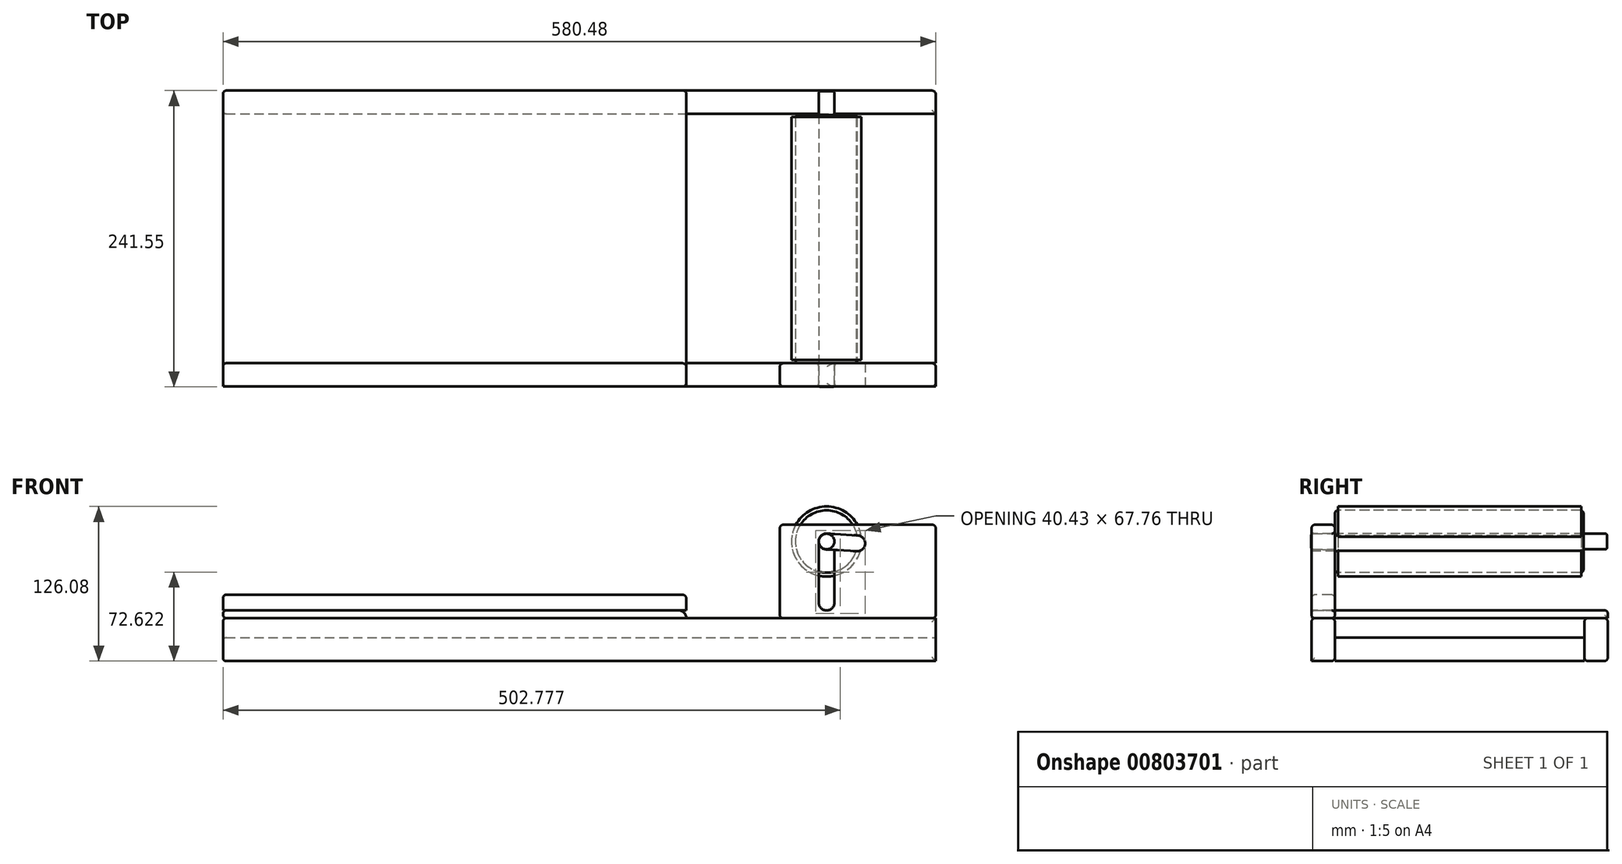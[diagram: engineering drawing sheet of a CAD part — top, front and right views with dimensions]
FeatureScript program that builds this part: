
annotation { "Feature Type Name" : "Feature", "Feature Type Description" : "" }
export const myFeature = defineFeature(function(context is Context, id is Id, definition is map)
    precondition{}
    {
        {
            var Q0;
            Q0=qCreatedBy(makeId("Top.planeOp"),FACE);
            var sketch = newSketch(context, id + "F0", { "sketchPlane" : qUnion([Q0])});
            skLineSegment(sketch, "E0.bottom", {"start": v(-381, 101.6) * mm, "end": v(381, 101.6) * mm});
            skLineSegment(sketch, "E0.top", {"start": v(-381, -101.6) * mm, "end": v(381, -101.6) * mm});
            skLineSegment(sketch, "E0.left", {"start": v(-381, 101.6) * mm, "end": v(-381, -101.6) * mm});
            skLineSegment(sketch, "E0.right", {"start": v(381, 101.6) * mm, "end": v(381, -101.6) * mm});
            skSolve(sketch);
        }
        {
            var Q0;
            Q0 = qSketchRegion(id + "F0", true);
            extrude(context, id + "F1", {"entities" : qUnion([Q0]), "depth" : 19.05 * mm, "offsetDistance" : 25.4 * mm});
        }
        {
            var Q0;
            Q0=makeQuery(id+"F1.opExtrude","CAP_FACE",FACE,{"disambiguationData":[OSD([sQuery(id+"F0.wireOp",EDGE,"E0.bottom"),sQuery(id+"F0.wireOp",EDGE,"E0.top"),sQuery(id+"F0.wireOp",EDGE,"E0.left"),sQuery(id+"F0.wireOp",EDGE,"E0.right")])],"isStart":true});
            var sketch = newSketch(context, id + "F2", { "sketchPlane" : qUnion([Q0])});
            skLineSegment(sketch, "E1", {"start": v(-381, 101.6) * mm, "end": v(-381, 120.65) * mm});
            skLineSegment(sketch, "E2", {"start": v(-381, 120.65) * mm, "end": v(381, 120.65) * mm});
            skLineSegment(sketch, "E3", {"start": v(381, 120.65) * mm, "end": v(381, 101.6) * mm});
            skLineSegment(sketch, "E4", {"start": v(381, 101.6) * mm, "end": v(-381, 101.6) * mm});
            skSolve(sketch);
        }
        {
            var Q0;
            Q0 = qSketchRegion(id + "F2", true);
            extrude(context, id + "F3", {"entities" : qUnion([Q0]), "oppositeDirection" : true, "depth" : 35.05 * mm, "offsetDistance" : 25.4 * mm});
        }
        {
            var Q0;
            Q0=makeQuery(id+"F3.opExtrude","CAP_FACE",FACE,{"disambiguationData":[OSD([sQuery(id+"F2.wireOp",EDGE,"E1"),sQuery(id+"F2.wireOp",EDGE,"E2"),sQuery(id+"F2.wireOp",EDGE,"E3"),sQuery(id+"F2.wireOp",EDGE,"E4")])],"isStart":false});
            var sketch = newSketch(context, id + "F4", { "sketchPlane" : qUnion([Q0])});
            skLineSegment(sketch, "E5", {"start": v(381, -101.6) * mm, "end": v(254, -101.6) * mm});
            skLineSegment(sketch, "E6", {"start": v(254, -101.6) * mm, "end": v(254, -120.65) * mm});
            skLineSegment(sketch, "E7", {"start": v(254, -120.65) * mm, "end": v(381, -120.65) * mm});
            skLineSegment(sketch, "E8", {"start": v(381, -120.65) * mm, "end": v(381, -101.6) * mm});
            skSolve(sketch);
        }
        {
            var Q0;
            Q0 = qSketchRegion(id + "F4", true);
            extrude(context, id + "F5", {"entities" : qUnion([Q0]), "depth" : 76.2 * mm, "offsetDistance" : 25.4 * mm});
        }
        {
            var Q0;
            Q0=makeQuery(id+"F3.boolean.opBoolean","MERGE",FACE,{"derivedFrom":[makeQuery(id+"F1.opExtrude","CAP_FACE",FACE,{"disambiguationData":[OSD([sQuery(id+"F0.wireOp",EDGE,"E0.bottom"),sQuery(id+"F0.wireOp",EDGE,"E0.top"),sQuery(id+"F0.wireOp",EDGE,"E0.left"),sQuery(id+"F0.wireOp",EDGE,"E0.right")])],"isStart":true}),makeQuery(id+"F3.opExtrude","CAP_FACE",FACE,{"disambiguationData":[OSD([sQuery(id+"F2.wireOp",EDGE,"E1"),sQuery(id+"F2.wireOp",EDGE,"E2"),sQuery(id+"F2.wireOp",EDGE,"E3"),sQuery(id+"F2.wireOp",EDGE,"E4")])],"isStart":true})]});
            var sketch = newSketch(context, id + "F6", { "sketchPlane" : qUnion([Q0])});
            skLineSegment(sketch, "E9", {"start": v(381, -101.6) * mm, "end": v(254, -101.6) * mm});
            skLineSegment(sketch, "E10", {"start": v(254, -101.6) * mm, "end": v(254, -120.65) * mm});
            skLineSegment(sketch, "E11", {"start": v(254, -120.65) * mm, "end": v(381, -120.65) * mm});
            skLineSegment(sketch, "E12", {"start": v(381, -120.65) * mm, "end": v(381, -101.6) * mm});
            skSolve(sketch);
        }
        {
            var Q0;
            Q0 = qSketchRegion(id + "F6", true);
            extrude(context, id + "F7", {"entities" : qUnion([Q0]), "oppositeDirection" : true, "depth" : 111.25 * mm, "offsetDistance" : 25.4 * mm});
        }
        {
            var Q0;
            Q0=makeQuery(id+"F3.boolean.opBoolean","MERGE",FACE,{"derivedFrom":[makeQuery(id+"F1.opExtrude","CAP_FACE",FACE,{"disambiguationData":[OSD([sQuery(id+"F0.wireOp",EDGE,"E0.bottom"),sQuery(id+"F0.wireOp",EDGE,"E0.top"),sQuery(id+"F0.wireOp",EDGE,"E0.left"),sQuery(id+"F0.wireOp",EDGE,"E0.right")])],"isStart":true}),makeQuery(id+"F3.opExtrude","CAP_FACE",FACE,{"disambiguationData":[OSD([sQuery(id+"F2.wireOp",EDGE,"E1"),sQuery(id+"F2.wireOp",EDGE,"E2"),sQuery(id+"F2.wireOp",EDGE,"E3"),sQuery(id+"F2.wireOp",EDGE,"E4")])],"isStart":true})]});
            var sketch = newSketch(context, id + "F8", { "sketchPlane" : qUnion([Q0])});
            skLineSegment(sketch, "E13", {"start": v(-381, -101.6) * mm, "end": v(-381, -120.65) * mm});
            skLineSegment(sketch, "E14", {"start": v(-381, -120.65) * mm, "end": v(381, -120.65) * mm});
            skLineSegment(sketch, "E15", {"start": v(381, -120.65) * mm, "end": v(381, -101.6) * mm});
            skLineSegment(sketch, "E16", {"start": v(381, -101.6) * mm, "end": v(-381, -101.6) * mm});
            skSolve(sketch);
        }
        {
            var Q0;
            Q0 = qSketchRegion(id + "F8", true);
            extrude(context, id + "F9", {"entities" : qUnion([Q0]), "oppositeDirection" : true, "depth" : 35.05 * mm, "offsetDistance" : 25.4 * mm});
        }
        {
            var Q0;
            Q0=makeQuery(id+"F9.opExtrude","CAP_FACE",FACE,{"disambiguationData":[OSD([sQuery(id+"F8.wireOp",EDGE,"E13"),sQuery(id+"F8.wireOp",EDGE,"E14"),sQuery(id+"F8.wireOp",EDGE,"E15"),sQuery(id+"F8.wireOp",EDGE,"E16")])],"isStart":false});
            var sketch = newSketch(context, id + "F10", { "sketchPlane" : qUnion([Q0])});
            skLineSegment(sketch, "E17", {"start": v(-381, 120.65) * mm, "end": v(-381, -120.65) * mm});
            skLineSegment(sketch, "E18", {"start": v(-381, -120.65) * mm, "end": v(177.8, -120.65) * mm});
            skLineSegment(sketch, "E19", {"start": v(177.8, -120.65) * mm, "end": v(177.8, 120.65) * mm});
            skLineSegment(sketch, "E20", {"start": v(177.8, 120.65) * mm, "end": v(-381, 120.65) * mm});
            skSolve(sketch);
        }
        {
            var Q0;
            Q0 = qSketchRegion(id + "F10", true);
            extrude(context, id + "F11", {"entities" : qUnion([Q0]), "depth" : 6.35 * mm, "offsetDistance" : 25.4 * mm});
        }
        {
            var Q0;
            Q0=makeQuery(id+"F11.opExtrude","CAP_FACE",FACE,{"disambiguationData":[OSD([sQuery(id+"F10.wireOp",EDGE,"E17"),sQuery(id+"F10.wireOp",EDGE,"E18"),sQuery(id+"F10.wireOp",EDGE,"E19"),sQuery(id+"F10.wireOp",EDGE,"E20")])],"isStart":false});
            var sketch = newSketch(context, id + "F12", { "sketchPlane" : qUnion([Q0])});
            skLineSegment(sketch, "E21", {"start": v(-381, -120.65) * mm, "end": v(-381, -101.6) * mm});
            skLineSegment(sketch, "E22", {"start": v(-381, -101.6) * mm, "end": v(177.8, -101.6) * mm});
            skLineSegment(sketch, "E23", {"start": v(177.8, -101.6) * mm, "end": v(177.8, -120.65) * mm});
            skLineSegment(sketch, "E24", {"start": v(177.8, -120.65) * mm, "end": v(-381, -120.65) * mm});
            skSolve(sketch);
        }
        {
            var Q0;
            Q0 = qSketchRegion(id + "F12", true);
            extrude(context, id + "F13", {"entities" : qUnion([Q0]), "depth" : 12.7 * mm, "offsetDistance" : 25.4 * mm});
        }
        {
            var Q0;
            Q0=makeQuery(id+"F11.opExtrude","CAP_EDGE",EDGE,{"disambiguationData":[OSD([sQuery(id+"F10.wireOp",EDGE,"E19")])],"isStart":false});
            fillet(context, id + "F14", {"entities" : qUnion([Q0]), "radius" : 6.35 * mm, "tangentPropagation" : true, "allowEdgeOverflow" : false});
        }
        {
            var Q0;
            Q0=makeQuery(id+"F5.opExtrude","CAP_EDGE",EDGE,{"disambiguationData":[OSD([sQuery(id+"F4.wireOp",EDGE,"E7")])],"isStart":false});
            var Q1;
            Q1=makeQuery(id+"F5.opExtrude","SWEPT_EDGE",EDGE,{"disambiguationData":[OSD([sQuery(id+"F2.wireOp",EDGE,"E2"),sQuery(id+"F4.wireOp",EDGE,"E6"),sQuery(id+"F4.wireOp",EDGE,"E7")])]});
            var Q2;
            Q2=makeQuery(id+"F5.opExtrude","SWEPT_EDGE",EDGE,{"disambiguationData":[OSD([sQuery(id+"F4.wireOp",EDGE,"E7"),sQuery(id+"F4.wireOp",EDGE,"E8")])]});
            var Q3;
            Q3=makeQuery(id+"F7.opExtrude","SWEPT_EDGE",EDGE,{"disambiguationData":[OSD([sQuery(id+"F0.wireOp",EDGE,"E0.right"),sQuery(id+"F2.wireOp",EDGE,"E3"),sQuery(id+"F6.wireOp",EDGE,"E9"),sQuery(id+"F6.wireOp",EDGE,"E12")])]});
            var Q4;
            Q4=makeQuery(id+"F7.opExtrude","CAP_EDGE",EDGE,{"disambiguationData":[OSD([sQuery(id+"F6.wireOp",EDGE,"E9")])],"isStart":false});
            var Q5;
            Q5=makeQuery(id+"F7.opExtrude","SWEPT_EDGE",EDGE,{"disambiguationData":[OSD([sQuery(id+"F0.wireOp",EDGE,"E0.bottom"),sQuery(id+"F6.wireOp",EDGE,"E9"),sQuery(id+"F6.wireOp",EDGE,"E10")])]});
            var Q6;
            Q6=makeQuery(id+"F5.opExtrude","SWEPT_EDGE",EDGE,{"disambiguationData":[OSD([sQuery(id+"F2.wireOp",EDGE,"E4"),sQuery(id+"F4.wireOp",EDGE,"E5"),sQuery(id+"F4.wireOp",EDGE,"E6")])]});
            var Q7;
            Q7=makeQuery(id+"F5.opExtrude","SWEPT_EDGE",EDGE,{"disambiguationData":[OSD([sQuery(id+"F4.wireOp",EDGE,"E5"),sQuery(id+"F4.wireOp",EDGE,"E8")])]});
            var Q8;
            Q8=makeQuery(id+"F5.opExtrude","CAP_EDGE",EDGE,{"disambiguationData":[OSD([sQuery(id+"F4.wireOp",EDGE,"E5")])],"isStart":false});
            var Q9;
            Q9=makeQuery(id+"F7.opExtrude","CAP_EDGE",EDGE,{"disambiguationData":[OSD([sQuery(id+"F6.wireOp",EDGE,"E11")])],"isStart":false});
            var Q10;
            Q10=makeQuery(id+"F7.opExtrude","SWEPT_EDGE",EDGE,{"disambiguationData":[OSD([sQuery(id+"F6.wireOp",EDGE,"E10"),sQuery(id+"F6.wireOp",EDGE,"E11")])]});
            var Q11;
            Q11=makeQuery(id+"F7.opExtrude","SWEPT_EDGE",EDGE,{"disambiguationData":[OSD([sQuery(id+"F6.wireOp",EDGE,"E11"),sQuery(id+"F6.wireOp",EDGE,"E12")])]});
            var Q12;
            Q12=makeQuery(id+"F7.opExtrude","CAP_EDGE",EDGE,{"disambiguationData":[OSD([sQuery(id+"F6.wireOp",EDGE,"E10")])],"isStart":false});
            var Q13;
            Q13=makeQuery(id+"F7.opExtrude","CAP_EDGE",EDGE,{"disambiguationData":[OSD([sQuery(id+"F6.wireOp",EDGE,"E12")])],"isStart":false});
            var Q14;
            Q14=makeQuery(id+"F5.opExtrude","CAP_EDGE",EDGE,{"disambiguationData":[OSD([sQuery(id+"F4.wireOp",EDGE,"E6")])],"isStart":false});
            var Q15;
            Q15=makeQuery(id+"F5.opExtrude","CAP_EDGE",EDGE,{"disambiguationData":[OSD([sQuery(id+"F4.wireOp",EDGE,"E8")])],"isStart":false});
            var Q16;
            Q16=makeQuery(id+"F9.opExtrude","CAP_EDGE",EDGE,{"disambiguationData":[OSD([sQuery(id+"F8.wireOp",EDGE,"E14")])],"isStart":true});
            var Q17;
            Q17=makeQuery(id+"F9.opExtrude","SWEPT_EDGE",EDGE,{"disambiguationData":[OSD([sQuery(id+"F8.wireOp",EDGE,"E14"),sQuery(id+"F8.wireOp",EDGE,"E15")])]});
            var Q18;
            Q18=makeQuery(id+"F3.opExtrude","SWEPT_FACE",FACE,{"disambiguationData":[OSD([sQuery(id+"F2.wireOp",EDGE,"E4")])]});
            var Q19;
            Q19=makeQuery(id+"F3.opExtrude","CAP_EDGE",EDGE,{"disambiguationData":[OSD([sQuery(id+"F2.wireOp",EDGE,"E2")])],"isStart":false});
            var Q20;
            Q20=makeQuery(id+"F9.opExtrude","CAP_EDGE",EDGE,{"disambiguationData":[OSD([sQuery(id+"F8.wireOp",EDGE,"E14")])],"isStart":false});
            var Q21;
            Q21=makeQuery(id+"F9.opExtrude","CAP_EDGE",EDGE,{"disambiguationData":[OSD([sQuery(id+"F8.wireOp",EDGE,"E16")])],"isStart":false});
            var Q22;
            Q22=makeQuery(id+"F13.opExtrude","CAP_EDGE",EDGE,{"disambiguationData":[OSD([sQuery(id+"F12.wireOp",EDGE,"E23")])],"isStart":false});
            var Q23;
            Q23=makeQuery(id+"F13.opExtrude","CAP_EDGE",EDGE,{"disambiguationData":[OSD([sQuery(id+"F12.wireOp",EDGE,"E24")])],"isStart":false});
            var Q24;
            Q24=makeQuery(id+"F13.opExtrude","SWEPT_EDGE",EDGE,{"disambiguationData":[OSD([sQuery(id+"F12.wireOp",EDGE,"E23"),sQuery(id+"F12.wireOp",EDGE,"E24")])]});
            var Q25;
            Q25=makeQuery(id+"F13.opExtrude","SWEPT_EDGE",EDGE,{"disambiguationData":[OSD([sQuery(id+"F10.wireOp",EDGE,"E19"),sQuery(id+"F12.wireOp",EDGE,"E22"),sQuery(id+"F12.wireOp",EDGE,"E23")])]});
            var Q26;
            Q26=makeQuery(id+"F11.opExtrude","CAP_EDGE",EDGE,{"disambiguationData":[OSD([sQuery(id+"F10.wireOp",EDGE,"E17")])],"isStart":false});
            var Q27;
            Q27=makeQuery(id+"F9.opExtrude","SWEPT_EDGE",EDGE,{"disambiguationData":[OSD([sQuery(id+"F0.wireOp",EDGE,"E0.left"),sQuery(id+"F2.wireOp",EDGE,"E1"),sQuery(id+"F8.wireOp",EDGE,"E13"),sQuery(id+"F8.wireOp",EDGE,"E16")])]});
            var Q28;
            Q28=makeQuery(id+"F9.opExtrude","SWEPT_EDGE",EDGE,{"disambiguationData":[OSD([sQuery(id+"F8.wireOp",EDGE,"E13"),sQuery(id+"F8.wireOp",EDGE,"E14")])]});
            var Q29;
            Q29=makeQuery(id+"F9.opExtrude","CAP_FACE",FACE,{"disambiguationData":[OSD([sQuery(id+"F8.wireOp",EDGE,"E13"),sQuery(id+"F8.wireOp",EDGE,"E14"),sQuery(id+"F8.wireOp",EDGE,"E15"),sQuery(id+"F8.wireOp",EDGE,"E16")])],"isStart":true});
            var Q30;
            Q30=makeQuery(id+"F13.opExtrude","CAP_EDGE",EDGE,{"disambiguationData":[OSD([sQuery(id+"F12.wireOp",EDGE,"E22")])],"isStart":false});
            fillet(context, id + "F15", {"entities" : qUnion([Q0, Q1, Q2, Q3, Q4, Q5, Q6, Q7, Q8, Q9, Q10, Q11, Q12, Q13, Q14, Q15, Q16, Q17, Q18, Q19, Q20, Q21, Q22, Q23, Q24, Q25, Q26, Q27, Q28, Q29, Q30]), "radius" : 3.05 * mm, "tangentPropagation" : true, "allowEdgeOverflow" : false});
        }
        {
            var Q0;
            Q0=makeQuery(id+"F5.opExtrude","SWEPT_FACE",FACE,{"disambiguationData":[OSD([sQuery(id+"F4.wireOp",EDGE,"E7")])]});
            var sketch = newSketch(context, id + "F16", { "sketchPlane" : qUnion([Q0])});
            skArc(sketch, "E25", {"start": v(298.58, 97.5) * mm, "mid": v(292.1, 103.98) * mm, "end": v(285.62, 97.5) * mm});
            skArc(sketch, "E26", {"start": v(285.62, 47.76) * mm, "mid": v(292.1, 41.28) * mm, "end": v(298.58, 47.76) * mm});
            skLineSegment(sketch, "E27", {"start": v(285.62, 97.5) * mm, "end": v(285.62, 47.76) * mm});
            skLineSegment(sketch, "E28", {"start": v(298.58, 97.5) * mm, "end": v(298.58, 47.76) * mm});
            skSolve(sketch);
        }
        {
            var Q0;
            Q0 = qSketchRegion(id + "F16", true);
            extrude(context, id + "F17", {"entities" : qUnion([Q0]), "operationType" : NewBodyOperationType.REMOVE, "oppositeDirection" : true, "depth" : 254 * mm, "offsetDistance" : 25.4 * mm});
        }
        {
            var Q0;
            Q0=makeQuery(id+"F5.opExtrude","SWEPT_FACE",FACE,{"disambiguationData":[OSD([sQuery(id+"F4.wireOp",EDGE,"E7")])]});
            var sketch = newSketch(context, id + "F18", { "sketchPlane" : qUnion([Q0])});
            skCircle(sketch, "E29", {"center": v(292.1, 97.5) * mm, "radius": 6.35 * mm});
            skSolve(sketch);
        }
        {
            var Q0;
            Q0 = qSketchRegion(id + "F18", true);
            extrude(context, id + "F19", {"entities" : qUnion([Q0]), "oppositeDirection" : true, "depth" : 241.3 * mm, "offsetDistance" : 25.4 * mm});
        }
        {
            var Q0;
            Q0=makeQuery(id+"F19.opExtrude","CAP_FACE",FACE,{"disambiguationData":[OSD([sQuery(id+"F18.wireOp",EDGE,"E29")])],"isStart":true});
            var Q1;
            Q1=makeQuery(id+"F19.opExtrude","CAP_FACE",FACE,{"disambiguationData":[OSD([sQuery(id+"F18.wireOp",EDGE,"E29")])],"isStart":false});
            fillet(context, id + "F20", {"entities" : qUnion([Q0, Q1]), "radius" : 3.05 * mm, "tangentPropagation" : true, "allowEdgeOverflow" : false});
        }
        {
            var Q0;
            Q0=makeQuery(id+"F5.opExtrude","SWEPT_FACE",FACE,{"disambiguationData":[OSD([sQuery(id+"F4.wireOp",EDGE,"E5")])]});
            var sketch = newSketch(context, id + "F21", { "sketchPlane" : qUnion([Q0])});
            skCircle(sketch, "E30", {"center": v(-292.1, 97.5) * mm, "radius": 25.4 * mm});
            skSolve(sketch);
        }
        {
            var Q0;
            Q0 = qSketchRegion(id + "F21", true);
            extrude(context, id + "F22", {"entities" : qUnion([Q0]), "depth" : 202.44 * mm, "offsetDistance" : 25.4 * mm});
        }
        {
            var Q0;
            Q0=makeQuery(id+"F22.opExtrude","CAP_FACE",FACE,{"disambiguationData":[OSD([sQuery(id+"F21.wireOp",EDGE,"E30")])],"isStart":false});
            fillet(context, id + "F23", {"entities" : qUnion([Q0]), "radius" : 2.54 * mm, "tangentPropagation" : true, "allowEdgeOverflow" : false});
        }
        {
            var Q0;
            Q0=makeQuery(id+"F22.opExtrude","CAP_EDGE",EDGE,{"disambiguationData":[OSD([sQuery(id+"F21.wireOp",EDGE,"E30")])],"isStart":true});
            fillet(context, id + "F24", {"entities" : qUnion([Q0]), "radius" : 2.54 * mm, "tangentPropagation" : true, "allowEdgeOverflow" : false});
        }
        {
            var Q0;
            Q0=makeQuery(id+"F22.opExtrude","CAP_FACE",FACE,{"disambiguationData":[OSD([sQuery(id+"F21.wireOp",EDGE,"E30")])],"isStart":true});
            var sketch = newSketch(context, id + "F25", { "sketchPlane" : qUnion([Q0])});
            skCircle(sketch, "E31", {"center": v(292.1, 97.5) * mm, "radius": 25.4 * mm});
            skCircle(sketch, "E32", {"center": v(292.1, 97.5) * mm, "radius": 28.58 * mm});
            skSolve(sketch);
        }
        {
            var Q0;
            Q0 = qSketchRegion(id + "F25", true);
            extrude(context, id + "F26", {"entities" : qUnion([Q0]), "oppositeDirection" : true, "depth" : 200.66 * mm, "offsetDistance" : 25.4 * mm});
        }
        {
            var Q0;
            Q0=makeQuery(id+"F22.opExtrude","CAP_FACE",FACE,{"disambiguationData":[OSD([sQuery(id+"F21.wireOp",EDGE,"E30")])],"isStart":true});
            var sketch = newSketch(context, id + "F27", { "sketchPlane" : qUnion([Q0])});
            skCircle(sketch, "E33", {"center": v(292.1, 97.5) * mm, "radius": 25.4 * mm});
            skCircle(sketch, "E34", {"center": v(292.1, 97.5) * mm, "radius": 30.03 * mm});
            skSolve(sketch);
        }
        {
            var Q0;
            Q0 = qSketchRegion(id + "F27", true);
            extrude(context, id + "F28", {"entities" : qUnion([Q0]), "operationType" : NewBodyOperationType.REMOVE, "oppositeDirection" : true, "depth" : 2.54 * mm, "offsetDistance" : 25.4 * mm});
        }
        {
            var Q0;
            Q0=makeQuery(id+"F3.opExtrude","SWEPT_FACE",FACE,{"disambiguationData":[OSD([sQuery(id+"F2.wireOp",EDGE,"E2")])]});
            var sketch = newSketch(context, id + "F29", { "sketchPlane" : qUnion([Q0])});
            skLineSegment(sketch, "E35", {"start": v(-402.68, 84.63) * mm, "end": v(-199.48, 84.63) * mm});
            skLineSegment(sketch, "E36", {"start": v(-199.48, 84.63) * mm, "end": v(-199.48, -54.52) * mm});
            skLineSegment(sketch, "E37", {"start": v(-199.48, -54.52) * mm, "end": v(-408.57, -54.52) * mm});
            skLineSegment(sketch, "E38", {"start": v(-408.57, -54.52) * mm, "end": v(-402.68, 84.63) * mm});
            skSolve(sketch);
        }
        {
            var Q0;
            Q0 = qSketchRegion(id + "F29", true);
            extrude(context, id + "F30", {"entities" : qUnion([Q0]), "operationType" : NewBodyOperationType.REMOVE, "oppositeDirection" : true, "depth" : 304.8 * mm, "offsetDistance" : 25.4 * mm});
        }
        {
            var Q0;
            Q0=makeQuery(id+"F30.boolean.opBoolean","INTERSECT",EDGE,{"derivedFrom":[makeQuery(id+"F9.opExtrude","SWEPT_FACE",FACE,{"disambiguationData":[OSD([sQuery(id+"F8.wireOp",EDGE,"E16")])]}),makeQuery(id+"F30.opExtrude","SWEPT_FACE",FACE,{"disambiguationData":[OSD([sQuery(id+"F29.wireOp",EDGE,"E36")])]})]});
            var Q1;
            Q1=makeQuery(id+"F30.boolean.opBoolean","INTERSECT",EDGE,{"derivedFrom":[makeQuery(id+"F1.opExtrude","CAP_FACE",FACE,{"disambiguationData":[OSD([sQuery(id+"F0.wireOp",EDGE,"E0.bottom"),sQuery(id+"F0.wireOp",EDGE,"E0.top"),sQuery(id+"F0.wireOp",EDGE,"E0.left"),sQuery(id+"F0.wireOp",EDGE,"E0.right")])],"isStart":false}),makeQuery(id+"F30.opExtrude","SWEPT_FACE",FACE,{"disambiguationData":[OSD([sQuery(id+"F29.wireOp",EDGE,"E36")])]})]});
            var Q2;
            Q2=makeQuery(id+"F30.boolean.opBoolean","INTERSECT",EDGE,{"derivedFrom":[makeQuery(id+"F3.boolean.opBoolean","MERGE",FACE,{"derivedFrom":[makeQuery(id+"F1.opExtrude","CAP_FACE",FACE,{"disambiguationData":[OSD([sQuery(id+"F0.wireOp",EDGE,"E0.bottom"),sQuery(id+"F0.wireOp",EDGE,"E0.top"),sQuery(id+"F0.wireOp",EDGE,"E0.left"),sQuery(id+"F0.wireOp",EDGE,"E0.right")])],"isStart":true}),makeQuery(id+"F3.opExtrude","CAP_FACE",FACE,{"disambiguationData":[OSD([sQuery(id+"F2.wireOp",EDGE,"E1"),sQuery(id+"F2.wireOp",EDGE,"E2"),sQuery(id+"F2.wireOp",EDGE,"E3"),sQuery(id+"F2.wireOp",EDGE,"E4")])],"isStart":true})]}),makeQuery(id+"F30.opExtrude","SWEPT_FACE",FACE,{"disambiguationData":[OSD([sQuery(id+"F29.wireOp",EDGE,"E36")])]})]});
            var Q3;
            Q3=makeQuery(id+"F30.boolean.opBoolean","INTERSECT",EDGE,{"derivedFrom":[makeQuery(id+"F11.opExtrude","CAP_FACE",FACE,{"disambiguationData":[OSD([sQuery(id+"F10.wireOp",EDGE,"E17"),sQuery(id+"F10.wireOp",EDGE,"E18"),sQuery(id+"F10.wireOp",EDGE,"E19"),sQuery(id+"F10.wireOp",EDGE,"E20")])],"isStart":true}),makeQuery(id+"F30.opExtrude","SWEPT_FACE",FACE,{"disambiguationData":[OSD([sQuery(id+"F29.wireOp",EDGE,"E36")])]})]});
            var Q4;
            Q4=makeQuery(id+"F30.boolean.opBoolean","INTERSECT",EDGE,{"derivedFrom":[makeQuery(id+"F11.opExtrude","CAP_FACE",FACE,{"disambiguationData":[OSD([sQuery(id+"F10.wireOp",EDGE,"E17"),sQuery(id+"F10.wireOp",EDGE,"E18"),sQuery(id+"F10.wireOp",EDGE,"E19"),sQuery(id+"F10.wireOp",EDGE,"E20")])],"isStart":false}),makeQuery(id+"F30.opExtrude","SWEPT_FACE",FACE,{"disambiguationData":[OSD([sQuery(id+"F29.wireOp",EDGE,"E36")])]})]});
            var Q5;
            {var subQ0=sQuery(id+"F29.wireOp",EDGE,"E36");Q5=makeQuery(id+"F30.boolean.opBoolean","COPY",EDGE,{"disambiguationData":[topologyDisambiguationEdgeConnected([makeQuery(id+"F13.opExtrude","SWEPT_FACE",FACE,{"disambiguationData":[OSD([sQuery(id+"F12.wireOp",EDGE,"E24")])]})])],"derivedFrom":makeQuery(id+"F30.opExtrude","CAP_EDGE",EDGE,{"disambiguationData":[OSD([subQ0])],"isStart":true})});}
            var Q6;
            Q6=makeQuery(id+"F30.boolean.opBoolean","INTERSECT",EDGE,{"derivedFrom":[makeQuery(id+"F13.opExtrude","SWEPT_FACE",FACE,{"disambiguationData":[OSD([sQuery(id+"F12.wireOp",EDGE,"E22")])]}),makeQuery(id+"F30.opExtrude","SWEPT_FACE",FACE,{"disambiguationData":[OSD([sQuery(id+"F29.wireOp",EDGE,"E36")])]})]});
            var Q7;
            Q7=makeQuery(id+"F11.opExtrude","CAP_EDGE",EDGE,{"disambiguationData":[OSD([sQuery(id+"F10.wireOp",EDGE,"E20")])],"isStart":false});
            var Q8;
            Q8=makeQuery(id+"F30.boolean.opBoolean","INTERSECT",EDGE,{"derivedFrom":[makeQuery(id+"F11.opExtrude","SWEPT_FACE",FACE,{"disambiguationData":[OSD([sQuery(id+"F10.wireOp",EDGE,"E20")])]}),makeQuery(id+"F30.opExtrude","SWEPT_FACE",FACE,{"disambiguationData":[OSD([sQuery(id+"F29.wireOp",EDGE,"E36")])]})]});
            var Q9;
            {var subQ0=sQuery(id+"F29.wireOp",EDGE,"E36");Q9=makeQuery(id+"F30.boolean.opBoolean","COPY",EDGE,{"disambiguationData":[topologyDisambiguationEdgeConnected([makeQuery(id+"F11.opExtrude","SWEPT_FACE",FACE,{"disambiguationData":[OSD([sQuery(id+"F10.wireOp",EDGE,"E18")])]})])],"derivedFrom":makeQuery(id+"F30.opExtrude","CAP_EDGE",EDGE,{"disambiguationData":[OSD([subQ0])],"isStart":true})});}
            fillet(context, id + "F31", {"entities" : qUnion([Q0, Q1, Q2, Q3, Q4, Q5, Q6, Q7, Q8, Q9]), "radius" : 2.54 * mm, "tangentPropagation" : true, "allowEdgeOverflow" : false});
        }
        {
            var Q0;
            Q0=makeQuery(id+"F7.opExtrude","SWEPT_FACE",FACE,{"disambiguationData":[OSD([sQuery(id+"F6.wireOp",EDGE,"E11")])]});
            var Q1;
            Q1=makeQuery(id+"F7.opExtrude","SWEPT_FACE",FACE,{"disambiguationData":[OSD([sQuery(id+"F6.wireOp",EDGE,"E9")])]});
            var Q2;
            Q2=makeQuery(id+"F5.opExtrude","SWEPT_FACE",FACE,{"disambiguationData":[OSD([sQuery(id+"F4.wireOp",EDGE,"E5")])]});
            var Q3;
            Q3=makeQuery(id+"F5.opExtrude","SWEPT_FACE",FACE,{"disambiguationData":[OSD([sQuery(id+"F4.wireOp",EDGE,"E7")])]});
            fillet(context, id + "F32", {"entities" : qUnion([Q0, Q1, Q2, Q3]), "radius" : 2.54 * mm, "tangentPropagation" : true, "allowEdgeOverflow" : false});
        }
        {
            var Q0;
            Q0=makeQuery(id+"F22.opExtrude","CAP_FACE",FACE,{"disambiguationData":[OSD([sQuery(id+"F21.wireOp",EDGE,"E30")])],"isStart":true});
            var sketch = newSketch(context, id + "F33", { "sketchPlane" : qUnion([Q0])});
            skCircle(sketch, "E39", {"center": v(292.1, 97.5) * mm, "radius": 25.4 * mm});
            skCircle(sketch, "E40", {"center": v(292.1, 97.5) * mm, "radius": 28.58 * mm});
            skSolve(sketch);
        }
        {
            var Q0;
            Q0 = qSketchRegion(id + "F33", true);
            extrude(context, id + "F34", {"entities" : qUnion([Q0]), "oppositeDirection" : true, "depth" : 200.66 * mm, "offsetDistance" : 25.4 * mm});
        }
        {
            var Q0;
            Q0=makeQuery(id+"F34.opExtrude","SWEPT_BODY",BODY,{"disambiguationData":[OSD([sQuery(id+"F33.wireOp",EDGE,"E39"),sQuery(id+"F33.wireOp",EDGE,"E40")])]});
            deleteBodies(context, id + "F35", {"entities" : qUnion([Q0])});
        }
        {
            var Q0;
            Q0=makeQuery(id+"F5.opExtrude","SWEPT_FACE",FACE,{"disambiguationData":[OSD([sQuery(id+"F4.wireOp",EDGE,"E7")])]});
            var sketch = newSketch(context, id + "F36", { "sketchPlane" : qUnion([Q0])});
            skArc(sketch, "E41", {"start": v(292.49, 103.97) * mm, "mid": v(285.63, 97.9) * mm, "end": v(291.71, 91.04) * mm});
            skArc(sketch, "E42", {"start": v(316.66, 89.55) * mm, "mid": v(323.51, 95.62) * mm, "end": v(317.43, 102.48) * mm});
            skLineSegment(sketch, "E43", {"start": v(292.49, 103.97) * mm, "end": v(317.43, 102.48) * mm});
            skLineSegment(sketch, "E44", {"start": v(291.71, 91.04) * mm, "end": v(316.66, 89.55) * mm});
            skSolve(sketch);
        }
        {
            var Q0;
            Q0 = qSketchRegion(id + "F36", true);
            extrude(context, id + "F37", {"entities" : qUnion([Q0]), "operationType" : NewBodyOperationType.REMOVE, "oppositeDirection" : true, "depth" : 254 * mm, "offsetDistance" : 25.4 * mm});
        }
        {
            var Q0;
            Q0=makeQuery(id+"F37.boolean.opBoolean","COPY",EDGE,{"derivedFrom":makeQuery(id+"F37.opExtrude","CAP_EDGE",EDGE,{"disambiguationData":[OSD([sQuery(id+"F36.wireOp",EDGE,"E43")])],"isStart":true})});
            var Q1;
            Q1=makeQuery(id+"F37.boolean.opBoolean","INTERSECT",EDGE,{"derivedFrom":[makeQuery(id+"F7.opExtrude","SWEPT_FACE",FACE,{"disambiguationData":[OSD([sQuery(id+"F6.wireOp",EDGE,"E9")])]}),makeQuery(id+"F37.opExtrude","SWEPT_FACE",FACE,{"disambiguationData":[OSD([sQuery(id+"F36.wireOp",EDGE,"E42")])]})]});
            fillet(context, id + "F38", {"entities" : qUnion([Q0, Q1]), "radius" : 2.54 * mm, "tangentPropagation" : true, "allowEdgeOverflow" : false});
        }
        {
            var Q0;
            Q0=makeQuery(id+"F22.opExtrude","CAP_FACE",FACE,{"disambiguationData":[OSD([sQuery(id+"F21.wireOp",EDGE,"E30")])],"isStart":true});
            var sketch = newSketch(context, id + "F39", { "sketchPlane" : qUnion([Q0])});
            skCircle(sketch, "E45", {"center": v(292.1, 97.5) * mm, "radius": 6.35 * mm});
            skSolve(sketch);
        }
        {
            var Q0;
            Q0 = qSketchRegion(id + "F39", true);
            extrude(context, id + "F40", {"entities" : qUnion([Q0]), "operationType" : NewBodyOperationType.ADD, "depth" : 19.3 * mm, "offsetDistance" : 25.4 * mm});
        }
        {
            var Q0;
            Q0=makeQuery(id+"F40.opExtrude","CAP_FACE",FACE,{"disambiguationData":[OSD([sQuery(id+"F39.wireOp",EDGE,"E45")])],"isStart":false});
            fillet(context, id + "F41", {"entities" : qUnion([Q0]), "radius" : 1.52 * mm, "tangentPropagation" : true, "allowEdgeOverflow" : false});
        }
        {
            var Q0;
            Q0=makeQuery(id+"F22.opExtrude","CAP_FACE",FACE,{"disambiguationData":[OSD([sQuery(id+"F21.wireOp",EDGE,"E30")])],"isStart":false});
            var sketch = newSketch(context, id + "F42", { "sketchPlane" : qUnion([Q0])});
            skCircle(sketch, "E46", {"center": v(-292.1, 97.5) * mm, "radius": 6.35 * mm});
            skSolve(sketch);
        }
        {
            var Q0;
            Q0 = qSketchRegion(id + "F42", true);
            extrude(context, id + "F43", {"entities" : qUnion([Q0]), "operationType" : NewBodyOperationType.ADD, "depth" : 19.3 * mm, "offsetDistance" : 25.4 * mm});
        }
        {
            var Q0;
            Q0=makeQuery(id+"F43.opExtrude","CAP_EDGE",EDGE,{"disambiguationData":[OSD([sQuery(id+"F42.wireOp",EDGE,"E46")])],"isStart":false});
            fillet(context, id + "F44", {"entities" : qUnion([Q0]), "radius" : 1.52 * mm, "tangentPropagation" : true, "allowEdgeOverflow" : false});
        }
        {
            var Q0;
            Q0=makeQuery(id+"F7.opExtrude","SWEPT_BODY",BODY,{"disambiguationData":[OSD([sQuery(id+"F6.wireOp",EDGE,"E9"),sQuery(id+"F6.wireOp",EDGE,"E10"),sQuery(id+"F6.wireOp",EDGE,"E11"),sQuery(id+"F6.wireOp",EDGE,"E12")])]});
            deleteBodies(context, id + "F45", {"entities" : qUnion([Q0])});
        }
    });
